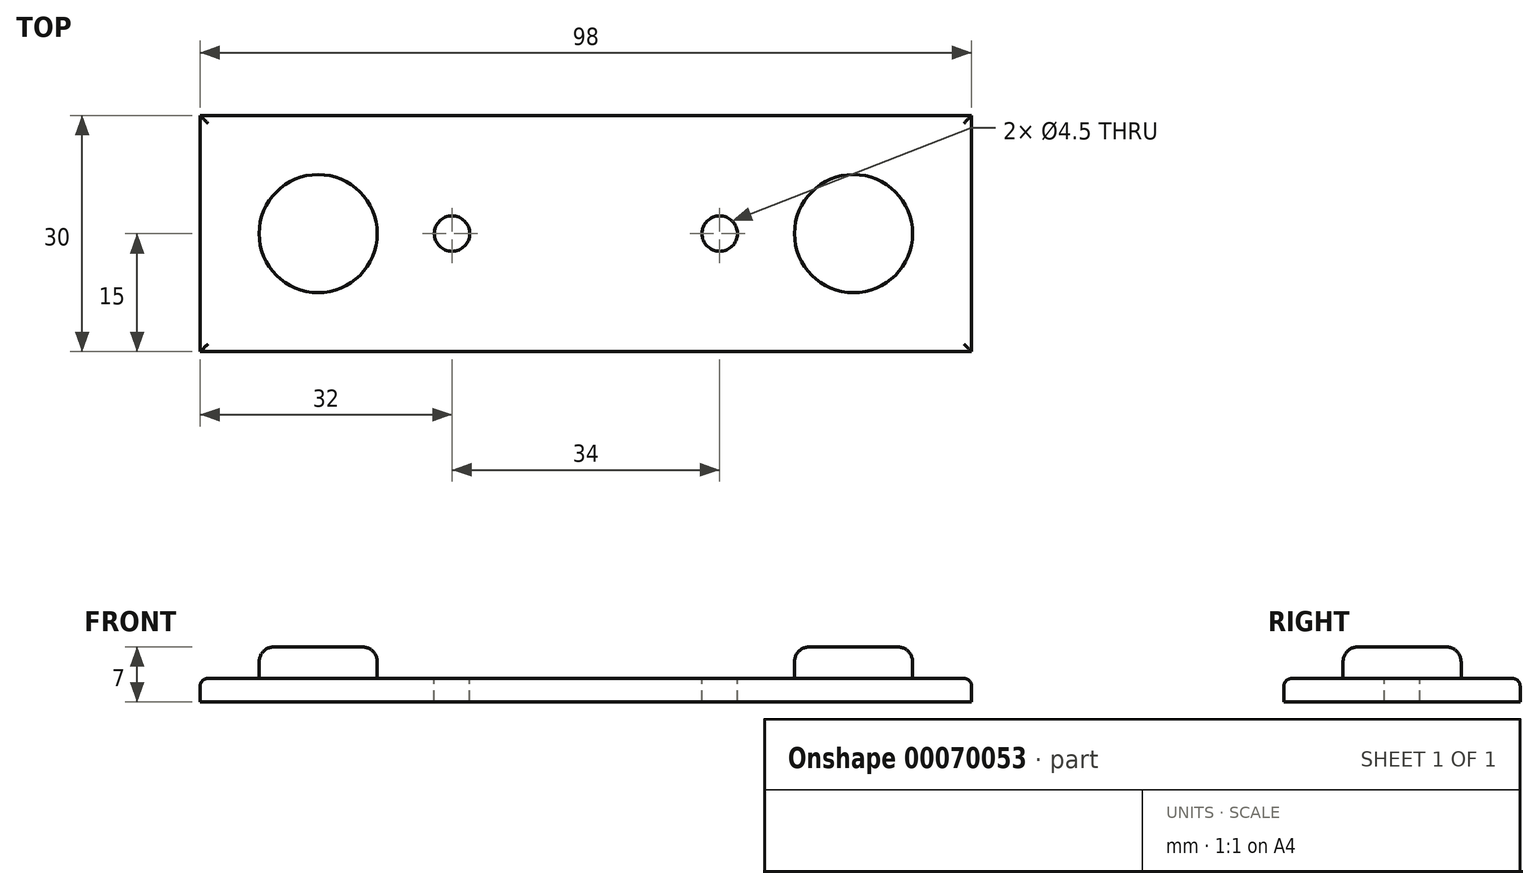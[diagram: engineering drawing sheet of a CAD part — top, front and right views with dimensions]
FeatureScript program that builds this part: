
annotation { "Feature Type Name" : "Feature", "Feature Type Description" : "" }
export const myFeature = defineFeature(function(context is Context, id is Id, definition is map)
    precondition{}
    {
        {
            var Q0;
            Q0=qCreatedBy(makeId("Top.planeOp"),FACE);
            var sketch = newSketch(context, id + "F0", { "sketchPlane" : qUnion([Q0])});
            skLineSegment(sketch, "E0.bottom", {"start": v(0, 0) * mm, "end": v(98, 0) * mm});
            skLineSegment(sketch, "E0.top", {"start": v(0, 30) * mm, "end": v(98, 30) * mm});
            skLineSegment(sketch, "E0.left", {"start": v(0, 0) * mm, "end": v(0, 30) * mm});
            skLineSegment(sketch, "E0.right", {"start": v(98, 0) * mm, "end": v(98, 30) * mm});
            skLineSegment(sketch, "E1", {"start": v(0, 15) * mm, "end": v(98, 15) * mm, "construction": true});
            skLineSegment(sketch, "E2", {"start": v(49, 30) * mm, "end": v(49, 0) * mm, "construction": true});
            skCircle(sketch, "E3", {"center": v(32, 15) * mm, "radius": 2.25 * mm});
            skCircle(sketch, "E4", {"center": v(66, 15) * mm, "radius": 2.25 * mm});
            skCircle(sketch, "E5", {"center": v(15, 15) * mm, "radius": 7.5 * mm});
            skCircle(sketch, "E6", {"center": v(83, 15) * mm, "radius": 7.5 * mm});
            skSolve(sketch);
        }
        {
            var Q0;
            Q0 = qSketchRegion(id + "F0", true);
            var Q1;
            Q1=makeQuery(id+"F0.imprint","IMPRINT",FACE,{"disambiguationData":[TD([[makeQuery(id+"F0.imprint","IMPRINT",EDGE,{"derivedFrom":sQuery(id+"F0.wireOp",EDGE,"E6")}),1.0]])]});
            var Q2;
            Q2=makeQuery(id+"F0.imprint","IMPRINT",FACE,{"disambiguationData":[TD([[makeQuery(id+"F0.imprint","IMPRINT",EDGE,{"derivedFrom":sQuery(id+"F0.wireOp",EDGE,"E5")}),1.0]])]});
            extrude(context, id + "F1", {"entities" : qUnion([Q0, Q1, Q2]), "oppositeDirection" : true, "depth" : 3 * mm});
        }
        {
            var Q0;
            Q0=makeQuery(id+"F0.imprint","IMPRINT",FACE,{"disambiguationData":[TD([[makeQuery(id+"F0.imprint","IMPRINT",EDGE,{"derivedFrom":sQuery(id+"F0.wireOp",EDGE,"E5")}),1.0]])]});
            var Q1;
            Q1=makeQuery(id+"F0.imprint","IMPRINT",FACE,{"disambiguationData":[TD([[makeQuery(id+"F0.imprint","IMPRINT",EDGE,{"derivedFrom":sQuery(id+"F0.wireOp",EDGE,"E6")}),1.0]])]});
            extrude(context, id + "F2", {"entities" : qUnion([Q0, Q1]), "operationType" : NewBodyOperationType.ADD, "depth" : 4 * mm});
        }
        {
            var Q0;
            Q0=makeQuery(id+"F2.opExtrude","CAP_EDGE",EDGE,{"disambiguationData":[OSD([sQuery(id+"F0.wireOp",EDGE,"E5")])],"isStart":false});
            var Q1;
            Q1=makeQuery(id+"F2.opExtrude","CAP_EDGE",EDGE,{"disambiguationData":[OSD([sQuery(id+"F0.wireOp",EDGE,"E6")])],"isStart":false});
            fillet(context, id + "F3", {"entities" : qUnion([Q0, Q1]), "radius" : 1.9 * mm, "tangentPropagation" : true, "allowEdgeOverflow" : false});
        }
        {
            var Q0;
            Q0=makeQuery(id+"F1.opExtrude","CAP_EDGE",EDGE,{"disambiguationData":[OSD([sQuery(id+"F0.wireOp",EDGE,"E0.top")])],"isStart":true});
            var Q1;
            Q1=makeQuery(id+"F1.opExtrude","CAP_EDGE",EDGE,{"disambiguationData":[OSD([sQuery(id+"F0.wireOp",EDGE,"E0.left")])],"isStart":true});
            var Q2;
            Q2=makeQuery(id+"F1.opExtrude","CAP_EDGE",EDGE,{"disambiguationData":[OSD([sQuery(id+"F0.wireOp",EDGE,"E0.right")])],"isStart":true});
            var Q3;
            Q3=makeQuery(id+"F1.opExtrude","CAP_EDGE",EDGE,{"disambiguationData":[OSD([sQuery(id+"F0.wireOp",EDGE,"E0.bottom")])],"isStart":true});
            fillet(context, id + "F4", {"entities" : qUnion([Q0, Q1, Q2, Q3]), "radius" : 1 * mm, "tangentPropagation" : true, "allowEdgeOverflow" : false});
        }
    });
